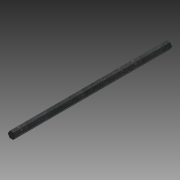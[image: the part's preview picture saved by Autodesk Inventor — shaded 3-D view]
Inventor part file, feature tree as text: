
AUTODESK INVENTOR PART (.ipt)
format: ipt  version: 2014 (Build 180170000, 170)  size: 77,312 bytes
history: native  units: in
note: dims shown in document units (in); Inventor stores cm internally (conversion verified against a paired STEP export)
features: extrude x1, sketch x1
ambient origin geometry x8: Origin, YZ Plane, XZ Plane, XY Plane, X Axis, Y Axis, Z Axis, Center Point
bodies: Solid1 (feature_tree)
feature tree (2):
  extrude  "Extrusion1"  Depth=9.5in TaperAngle=0.0deg
  sketch  "Sketch1"  dims[d0=0.375in d1=9.5in d2=0.0in]
